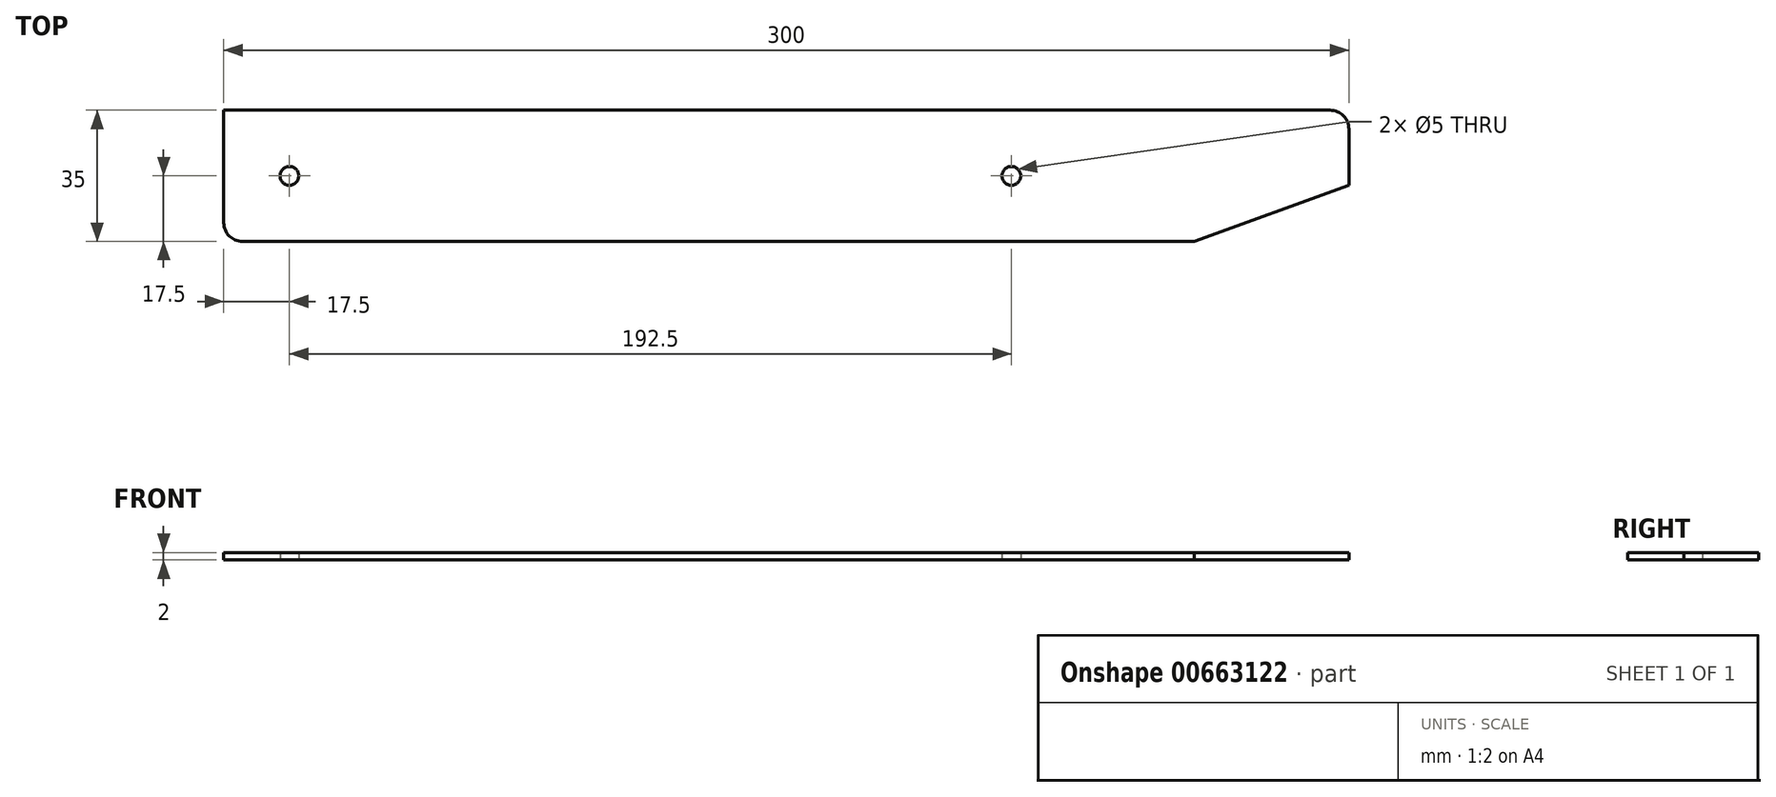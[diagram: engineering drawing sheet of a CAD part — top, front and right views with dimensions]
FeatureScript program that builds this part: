
annotation { "Feature Type Name" : "Feature", "Feature Type Description" : "" }
export const myFeature = defineFeature(function(context is Context, id is Id, definition is map)
    precondition{}
    {
        {
            var Q0;
            Q0=qCreatedBy(makeId("Top.planeOp"),FACE);
            var sketch = newSketch(context, id + "F0", { "sketchPlane" : qUnion([Q0])});
            skLineSegment(sketch, "E0.bottom", {"start": v(0, 0) * mm, "end": v(300, 0) * mm});
            skLineSegment(sketch, "E0.top", {"start": v(0, 35) * mm, "end": v(300, 35) * mm});
            skLineSegment(sketch, "E0.left", {"start": v(0, 0) * mm, "end": v(0, 35) * mm});
            skLineSegment(sketch, "E0.right", {"start": v(300, 0) * mm, "end": v(300, 35) * mm});
            skCircle(sketch, "E1", {"center": v(17.5, 17.5) * mm, "radius": 2.5 * mm});
            skPoint(sketch, "E1.centerSnap0", {"position": v(0, 17.5) * mm});
            skCircle(sketch, "E2", {"center": v(210, 17.5) * mm, "radius": 2.5 * mm});
            skPoint(sketch, "E2.centerSnap0", {"position": v(300, 17.5) * mm});
            skSolve(sketch);
        }
        {
            var Q0;
            Q0=makeQuery(id+"F0.imprint","IMPRINT",FACE,{"disambiguationData":[TD([[makeQuery(id+"F0.imprint","IMPRINT",EDGE,{"derivedFrom":sQuery(id+"F0.wireOp",EDGE,"E0.bottom")}),1.0]])]});
            extrude(context, id + "F1", {"entities" : qUnion([Q0]), "depth" : 2 * mm, "offsetDistance" : 25 * mm});
        }
        {
            var Q0;
            Q0=makeQuery(id+"F1.opExtrude","SWEPT_EDGE",EDGE,{"disambiguationData":[OSD([sQuery(id+"F0.wireOp",EDGE,"E0.bottom"),sQuery(id+"F0.wireOp",EDGE,"E0.left")])]});
            var Q1;
            Q1=makeQuery(id+"F1.opExtrude","SWEPT_EDGE",EDGE,{"disambiguationData":[OSD([sQuery(id+"F0.wireOp",EDGE,"E0.top"),sQuery(id+"F0.wireOp",EDGE,"E0.right")])]});
            fillet(context, id + "F2", {"entities" : qUnion([Q0, Q1]), "radius" : 5 * mm, "tangentPropagation" : true, "allowEdgeOverflow" : false});
        }
        {
            var Q0;
            Q0=makeQuery(id+"F1.opExtrude","SWEPT_EDGE",EDGE,{"disambiguationData":[OSD([sQuery(id+"F0.wireOp",EDGE,"E0.bottom"),sQuery(id+"F0.wireOp",EDGE,"E0.right")])]});
            chamfer(context, id + "F3", {"entities" : qUnion([Q0]), "chamferType" : ChamferType.OFFSET_ANGLE, "width" : 15 * mm, "oppositeDirection" : false, "angle" : 70 * degree, "tangentPropagation" : true});
        }
    });
